# Revit family: Hager-Pablo-IP40-Transparent_Door-sistema-NoHosted-IT-it
name_source: partatom
category: Electrical Equipment
units: mm (PartAtom-declared; Revit-internal decimal feet)

## family parameters
Always vertical = Yes
Cut with Voids When Loaded = No
Panel Configuration = Two Columns, Circuits Across
Part Type = Panelboard
Room Calculation Point = No
Round Connector Dimension = Use Diameter
Shared = No
Work Plane-Based = Yes

## types (13) — shared parameters
Default Elevation = 1219 mm
EF000003 - Tipo di montaggio = EV000384 - A parete
EF000118 - con piastra di montaggio = No
EF000339 - tipo di copertura = EV004216 - porta
EF001062 - esecuzione EMC = No
EF001088 - possibilità di applicazione = No
EF001134 - barra DIN = Yes
EF001596 - Attacco Lampada = EV000139 - plastica
EF004462 - tipo di chiusura = EV000154 - altri
EF005474 - grado di protezione (IP) = EV006415 - IP40
EF006244 - coperchio/porta trasparente = Yes
EF006306 - con serratura = No
EF015776 - Morsettiera di terra = No
EF015777 - Morsettiera neutra = No
EF015941 - Segnale di passaggio porta = Yes
HG000001 - Numero di colonne = 1
HG000002 - Con porta = Yes
HG000003 - Gamma = Pablo
HG000005 - Spessore = 3 mm  [stored 0.00984252 ft]
HG000006 - Ad incasso = No
HG000009 - Porta doppia a battente = No
HG000010 - Porte asimmetriche = No
HG000011 - File vuote nella parte basse = No
HG000017 - Distanza tra i poli = 18 mm  [stored 0.0590551 ft]
Manufacturer = Hager
Type Comments = Pablo
zero-valued in all types: EF000218 - profondità di incasso, EF000332 - Altezza della parte incassata, EF000846 - larghezza di montaggio, HG000007 - Numero di colonne vuote, HG000008 - Numero di file vuote

## per-type parameters (varying)
| type | EF000007 - colore | EF000008 - Larghezza | EF000040 - Altezza | EF000049 - profondità | EF000116 - numero RAL | EF000266 - numero di file | EF001131 - profondità interna | EF002950 - Numero moduli DIN | EF009212 - esecuzione coperchio | HG000004 - Codice produttore | Model |
| A parete IP40 L110 A140 P86 4 Unità di divisione - B04000 | EV000270 - grigio | 110 mm  [stored 0.360892 ft] | 140 mm  [stored 0.459318 ft] | 86 mm  [stored 0.282152 ft] | 7035 | 1 | 86 mm  [stored 0.282152 ft] | 4 | EV009916 - con taglio | B04000 | B04000 |
| A parete IP40 L210 A200 P103 8 Unità di divisione - B04002 | EV000270 - grigio | 210 mm  [stored 0.688976 ft] | 200 mm  [stored 0.656168 ft] | 103 mm  [stored 0.337927 ft] | 7035 | 1 | 103 mm  [stored 0.337927 ft] | 8 | EV009916 - con taglio | B04002 | B04002 |
| A parete IP40 L210 A200 P103 8 Unità di divisione - B04083 | EV000270 - grigio | 210 mm  [stored 0.688976 ft] | 200 mm  [stored 0.656168 ft] | 103 mm  [stored 0.337927 ft] | 9001 | 1 | 48 mm  [stored 0.15748 ft] | 8 | EV000116 - chiuso | B04083 | B04083 |
| A parete IP40 L300 A250 P113 12 Unità di divisione - B04010 | EV000270 - grigio | 300 mm | 250 mm  [stored 0.82021 ft] | 113 mm  [stored 0.370735 ft] | 7035 | 1 | 113 mm  [stored 0.370735 ft] | 12 | EV009916 - con taglio | B04010 | B04010 |
| A parete IP40 L300 A250 P113 12 Unità di divisione - B04084 | EV000202 - bianco | 300 mm | 250 mm  [stored 0.82021 ft] | 113 mm  [stored 0.370735 ft] | 9001 | 1 | 48 mm  [stored 0.15748 ft] | 12 | EV000116 - chiuso | B04084 | B04084 |
| A parete IP40 L300 A400 P113 12 Unità di divisione - B04020 | EV000270 - grigio | 300 mm | 400 mm  [stored 1.31234 ft] | 113 mm  [stored 0.370735 ft] | 7035 | 2 | 113 mm  [stored 0.370735 ft] | 12 | EV009916 - con taglio | B04020 | B04020 |
| A parete IP40 L300 A400 P113 12 Unità di divisione - B04086 | EV000202 - bianco | 300 mm | 400 mm  [stored 1.31234 ft] | 113 mm  [stored 0.370735 ft] | 9001 | 2 | 48 mm  [stored 0.15748 ft] | 12 | EV000116 - chiuso | B04086 | B04086 |
| A parete IP40 L408 A275 P137 18 Unità di divisione - B04011 | EV000270 - grigio | 408 mm | 275 mm | 137 mm  [stored 0.449475 ft] | 7035 | 1 | 137 mm  [stored 0.449475 ft] | 18 | EV009916 - con taglio | B04011 | B04011 |
| A parete IP40 L408 A275 P137 18 Unità di divisione - B04085 | EV000202 - bianco | 408 mm | 275 mm | 137 mm  [stored 0.449475 ft] | 9001 | 1 | 48 mm  [stored 0.15748 ft] | 18 | EV000116 - chiuso | B04085 | B04085 |
| A parete IP40 L408 A450 P137 18 Unità di divisione - B04021 | EV000270 - grigio | 408 mm | 450 mm  [stored 1.47638 ft] | 137 mm  [stored 0.449475 ft] | 7035 | 2 | 137 mm  [stored 0.449475 ft] | 18 | EV009916 - con taglio | B04021 | B04021 |
| A parete IP40 L408 A450 P137 18 Unità di divisione - B04089 | EV000270 - grigio | 408 mm | 450 mm  [stored 1.47638 ft] | 137 mm  [stored 0.449475 ft] | 9001 | 2 | 48 mm  [stored 0.15748 ft] | 18 | EV000116 - chiuso | B04089 | B04089 |
| A parete IP40 L408 A625 P137 18 Unità di divisione - B04022 | EV000270 - grigio | 408 mm | 625 mm  [stored 2.05052 ft] | 137 mm  [stored 0.449475 ft] | 7035 | 3 | 137 mm  [stored 0.449475 ft] | 18 | EV009916 - con taglio | B04022 | B04022 |
| A parete IP40 L408 A625 P137 18 Unità di divisione - B04090 | EV000202 - bianco | 408 mm | 625 mm  [stored 2.05052 ft] | 137 mm  [stored 0.449475 ft] | 9001 | 3 | 48 mm  [stored 0.15748 ft] | 18 | EV000116 - chiuso | B04090 | B04090 |

note: [stored X ft] marks values corroborated as IEEE doubles in the binary element streams (Revit-internal decimal feet)

## geometry (parser evidence)
native form markers: Sweep x13
no freeform markers — native parametric forms only
